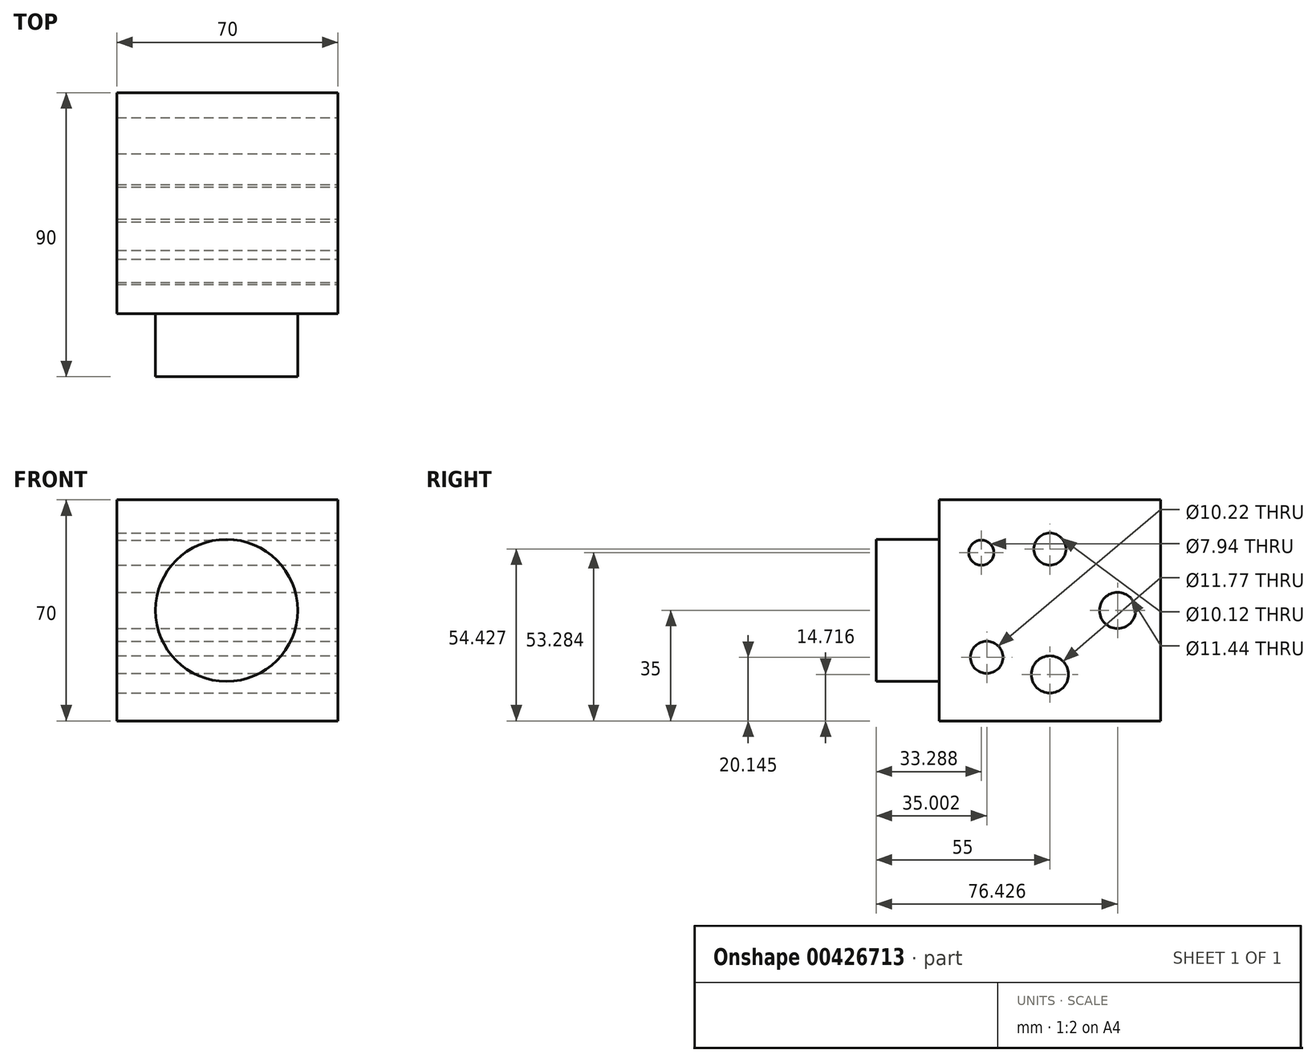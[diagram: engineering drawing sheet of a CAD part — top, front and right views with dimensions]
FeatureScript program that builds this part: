
annotation { "Feature Type Name" : "Feature", "Feature Type Description" : "" }
export const myFeature = defineFeature(function(context is Context, id is Id, definition is map)
    precondition{}
    {
        {
            var Q0;
            Q0=qCreatedBy(makeId("Top.planeOp"),FACE);
            var sketch = newSketch(context, id + "F0", { "sketchPlane" : qUnion([Q0])});
            skLineSegment(sketch, "E0.bottom", {"start": v(35, 35) * mm, "end": v(-35, 35) * mm});
            skLineSegment(sketch, "E0.top", {"start": v(35, -35) * mm, "end": v(-35, -35) * mm});
            skLineSegment(sketch, "E0.left", {"start": v(35, 35) * mm, "end": v(35, -35) * mm});
            skLineSegment(sketch, "E0.right", {"start": v(-35, 35) * mm, "end": v(-35, -35) * mm});
            skPoint(sketch, "E0.middle", {"position": v(0, 0) * mm});
            skSolve(sketch);
        }
        {
            var Q0;
            Q0 = qSketchRegion(id + "F0", true);
            extrude(context, id + "F1", {"entities" : qUnion([Q0]), "endBound" : BoundingType.SYMMETRIC, "depth" : 70 * mm});
        }
        {
            var Q0;
            Q0=makeQuery(id+"F1.opExtrude","SWEPT_FACE",FACE,{"disambiguationData":[OSD([sQuery(id+"F0.wireOp",EDGE,"E0.top")])]});
            var sketch = newSketch(context, id + "F2", { "sketchPlane" : qUnion([Q0])});
            skCircle(sketch, "E1", {"center": v(-0.29, 0) * mm, "radius": 22.5 * mm});
            skSolve(sketch);
        }
        {
            var Q0;
            Q0 = qSketchRegion(id + "F2", true);
            extrude(context, id + "F3", {"entities" : qUnion([Q0]), "operationType" : NewBodyOperationType.ADD, "depth" : 20 * mm});
        }
        {
            var Q0;
            Q0=makeQuery(id+"F1.opExtrude","SWEPT_FACE",FACE,{"disambiguationData":[OSD([sQuery(id+"F0.wireOp",EDGE,"E0.left")])]});
            var sketch = newSketch(context, id + "F4", { "sketchPlane" : qUnion([Q0])});
            skCircle(sketch, "E2", {"center": v(21.43, 0) * mm, "radius": 5.72 * mm});
            skCircle(sketch, "E3", {"center": v(0, 19.43) * mm, "radius": 5.06 * mm});
            skCircle(sketch, "E4", {"center": v(0, -20.28) * mm, "radius": 5.88 * mm});
            skCircle(sketch, "E5", {"center": v(-21.71, 18.28) * mm, "radius": 3.97 * mm});
            skCircle(sketch, "E6", {"center": v(-20, -14.86) * mm, "radius": 5.11 * mm});
            skSolve(sketch);
        }
        {
            var Q0;
            Q0 = qSketchRegion(id + "F4", true);
            extrude(context, id + "F5", {"entities" : qUnion([Q0]), "operationType" : NewBodyOperationType.REMOVE, "oppositeDirection" : true, "depth" : 70 * mm});
        }
    });
